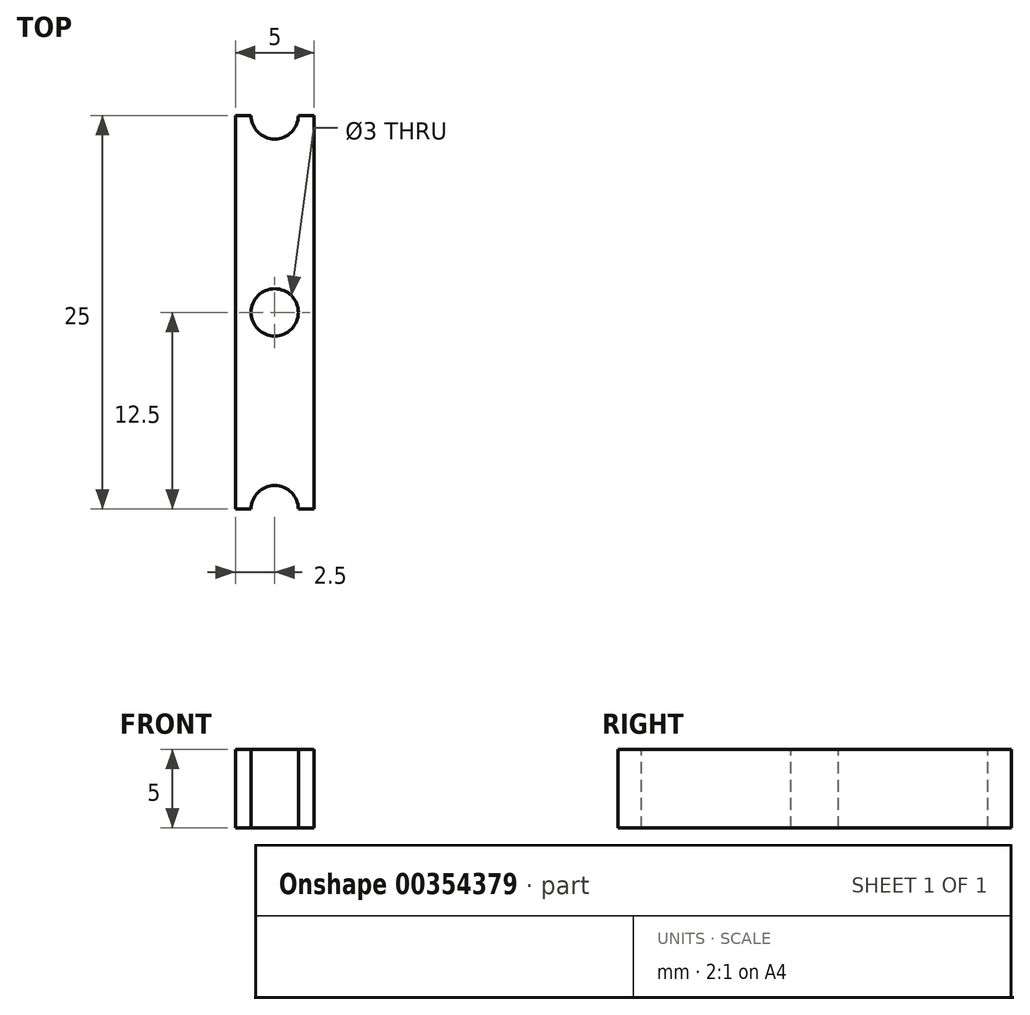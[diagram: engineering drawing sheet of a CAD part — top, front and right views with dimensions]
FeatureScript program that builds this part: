
annotation { "Feature Type Name" : "Feature", "Feature Type Description" : "" }
export const myFeature = defineFeature(function(context is Context, id is Id, definition is map)
    precondition{}
    {
        {
            assignVariable(context, id + "F0", {"name" : "height", "anyValue" : 5});
        }
        {
            var Q0;
            Q0=qCreatedBy(makeId("Top.planeOp"),FACE);
            var sketch = newSketch(context, id + "F1", { "sketchPlane" : qUnion([Q0])});
            skLineSegment(sketch, "E0.bottom", {"start": v(0, 0) * mm, "end": v(5, 0) * mm});
            skLineSegment(sketch, "E0.top", {"start": v(0, 25) * mm, "end": v(5, 25) * mm});
            skLineSegment(sketch, "E0.left", {"start": v(0, 0) * mm, "end": v(0, 25) * mm});
            skLineSegment(sketch, "E0.right", {"start": v(5, 0) * mm, "end": v(5, 25) * mm});
            skSolve(sketch);
        }
        {
            var Q0;
            Q0 = qSketchRegion(id + "F1", true);
            extrude(context, id + "F2", {"entities" : qUnion([Q0]), "depth" : (getVariable(context, 'height')) * mm, "offsetDistance" : 25 * mm});
        }
        {
            var Q0;
            Q0=makeQuery(id+"F2.opExtrude","CAP_FACE",FACE,{"disambiguationData":[OSD([sQuery(id+"F1.wireOp",EDGE,"E0.bottom"),sQuery(id+"F1.wireOp",EDGE,"E0.top"),sQuery(id+"F1.wireOp",EDGE,"E0.left"),sQuery(id+"F1.wireOp",EDGE,"E0.right")])],"isStart":false});
            var sketch = newSketch(context, id + "F3", { "sketchPlane" : qUnion([Q0])});
            skPoint(sketch, "E1", {"position": v(2.5, 0) * mm});
            skLineSegment(sketch, "E2", {"start": v(2.5, 0) * mm, "end": v(2.5, 25) * mm, "construction": true});
            skPoint(sketch, "E3", {"position": v(2.5, 12.5) * mm});
            skCircle(sketch, "E4", {"center": v(2.5, 12.5) * mm, "radius": 1.5 * mm});
            skLineSegment(sketch, "E5", {"start": v(4, 12.5) * mm, "end": v(4, 0) * mm, "construction": true});
            skArc(sketch, "E6", {"start": v(4, 0) * mm, "mid": v(2.5, 1.5) * mm, "end": v(1, 0) * mm});
            skLineSegment(sketch, "E7", {"start": v(4, 0) * mm, "end": v(1, 0) * mm});
            skLineSegment(sketch, "E8", {"start": v(5, 12.5) * mm, "end": v(0, 12.5) * mm, "construction": true});
            skArc(sketch, "E9.MirrorCS", {"start": v(4, 25) * mm, "mid": v(2.5, 23.5) * mm, "end": v(1, 25) * mm});
            skLineSegment(sketch, "E10.MirrorCS", {"start": v(4, 25) * mm, "end": v(1, 25) * mm});
            skSolve(sketch);
        }
        {
            var Q0;
            Q0 = qSketchRegion(id + "F3", true);
            extrude(context, id + "F4", {"entities" : qUnion([Q0]), "operationType" : NewBodyOperationType.REMOVE, "endBound" : BoundingType.THROUGH_ALL, "oppositeDirection" : true, "depth" : 25 * mm, "offsetDistance" : 25 * mm});
        }
    });
